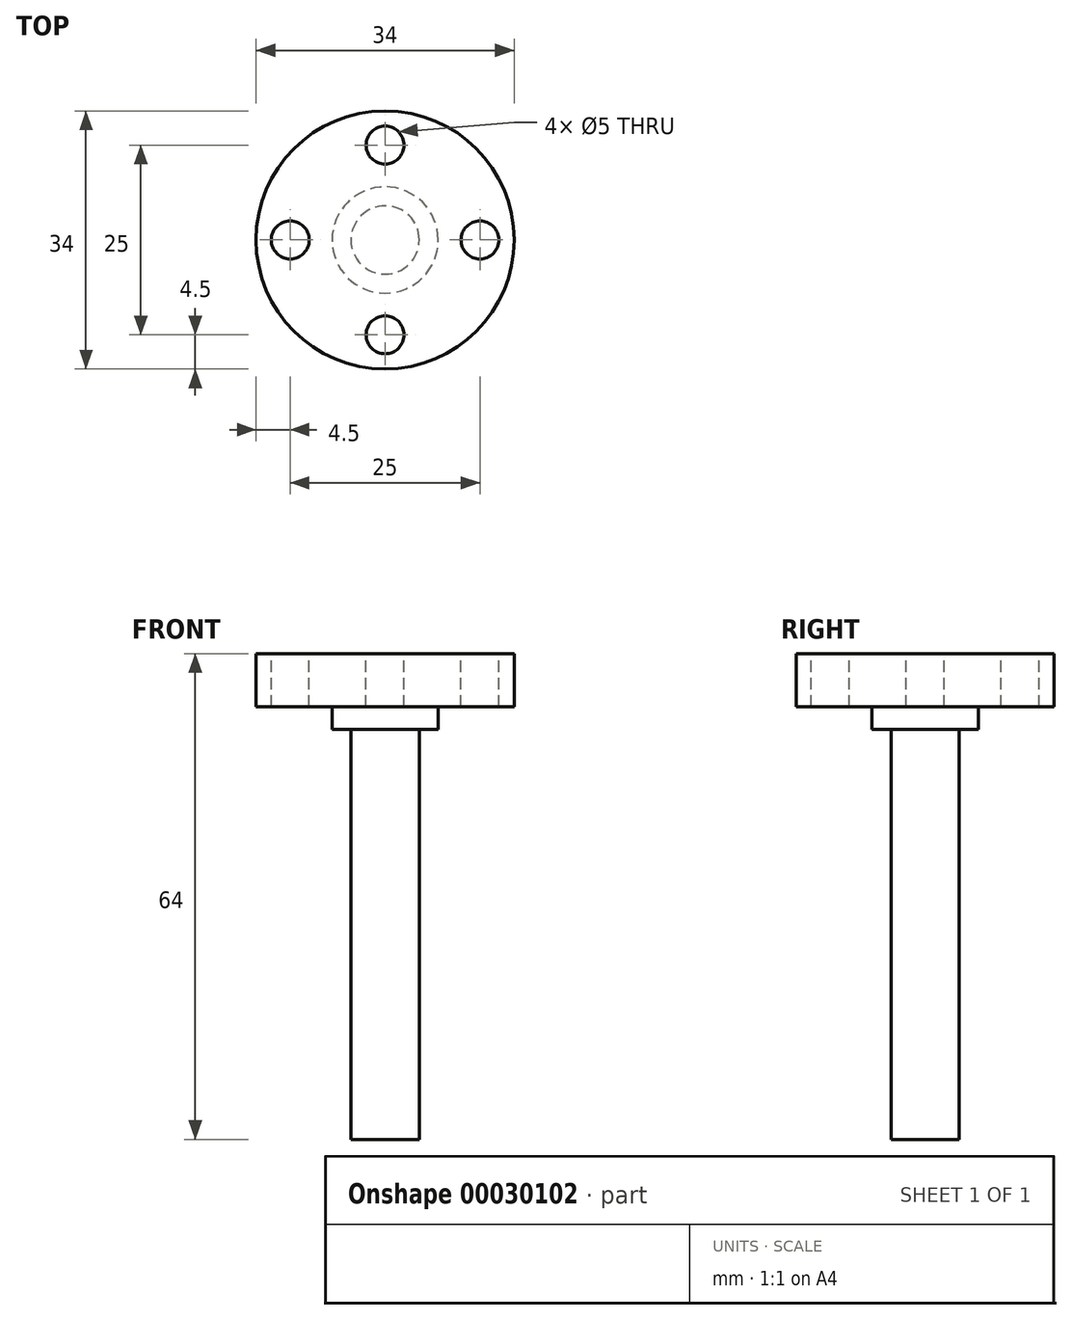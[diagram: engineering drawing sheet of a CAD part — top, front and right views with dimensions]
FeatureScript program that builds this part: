
annotation { "Feature Type Name" : "Feature", "Feature Type Description" : "" }
export const myFeature = defineFeature(function(context is Context, id is Id, definition is map)
    precondition{}
    {
        {
            var Q0;
            Q0=qCreatedBy(makeId("Right.planeOp"),FACE);
            var sketch = newSketch(context, id + "F0", { "sketchPlane" : qUnion([Q0])});
            skLineSegment(sketch, "E0", {"start": v(0, 0) * mm, "end": v(4.5, 0) * mm});
            skLineSegment(sketch, "E1", {"start": v(4.5, 0) * mm, "end": v(4.5, 54) * mm});
            skLineSegment(sketch, "E2", {"start": v(4.5, 54) * mm, "end": v(7, 54) * mm});
            skLineSegment(sketch, "E3", {"start": v(7, 54) * mm, "end": v(7, 57) * mm});
            skLineSegment(sketch, "E4", {"start": v(7, 57) * mm, "end": v(17, 57) * mm});
            skLineSegment(sketch, "E5", {"start": v(17, 57) * mm, "end": v(17, 64) * mm});
            skLineSegment(sketch, "E6", {"start": v(17, 64) * mm, "end": v(0, 64) * mm});
            skLineSegment(sketch, "E7", {"start": v(0, 64) * mm, "end": v(0, 0) * mm, "construction": true});
            skLineSegment(sketch, "E8", {"start": v(0, 64) * mm, "end": v(0, 0) * mm});
            skSolve(sketch);
        }
        {
            var Q0;
            Q0=makeQuery(id+"F0.imprint","IMPRINT",FACE,{"disambiguationData":[TD([[makeQuery(id+"F0.imprint","IMPRINT",EDGE,{"derivedFrom":sQuery(id+"F0.wireOp",EDGE,"E0")}),1.0]])]});
            var Q1;
            Q1=sQuery(id+"F0.wireOp",EDGE,"E8");
            revolve(context, id + "F1", {"entities" : qUnion([Q0]), "axis" : qUnion([Q1]), "revolveType" : RevolveType.FULL});
        }
        {
            var Q0;
            Q0=makeQuery(id+"F1.opRevolve","SWEPT_FACE",FACE,{"disambiguationData":[OSD([sQuery(id+"F0.wireOp",EDGE,"E6")])]});
            var sketch = newSketch(context, id + "F2", { "sketchPlane" : qUnion([Q0])});
            skCircle(sketch, "E9", {"center": v(0, 12.5) * mm, "radius": 2.25 * mm});
            skCircle(sketch, "E10", {"center": v(0, -12.5) * mm, "radius": 2.25 * mm});
            skCircle(sketch, "E11", {"center": v(12.5, 0) * mm, "radius": 2.25 * mm});
            skCircle(sketch, "E12", {"center": v(-12.5, 0) * mm, "radius": 2.25 * mm});
            skCircle(sketch, "E13", {"center": v(0, 0) * mm, "radius": 12.5 * mm, "construction": true});
            skSolve(sketch);
        }
        {
            var Q0;
            Q0=sQuery(id+"F2.wireOp",VERTEX,"E12.center");
            var Q1;
            Q1=sQuery(id+"F2.wireOp",VERTEX,"E10.center");
            var Q2;
            Q2=sQuery(id+"F2.wireOp",VERTEX,"E11.center");
            var Q3;
            Q3=sQuery(id+"F2.wireOp",VERTEX,"E9.center");
            var Q4;
            Q4=makeQuery(id+"F1.opRevolve","SWEPT_BODY",BODY,{"disambiguationData":[OSD([sQuery(id+"F0.wireOp",EDGE,"E0"),sQuery(id+"F0.wireOp",EDGE,"E1"),sQuery(id+"F0.wireOp",EDGE,"E2"),sQuery(id+"F0.wireOp",EDGE,"E3"),sQuery(id+"F0.wireOp",EDGE,"E4"),sQuery(id+"F0.wireOp",EDGE,"E5"),sQuery(id+"F0.wireOp",EDGE,"E6"),sQuery(id+"F0.wireOp",EDGE,"E8")])]});
            hole(context, id + "F3", {"style" : HoleStyle.SIMPLE, "holeDiameter" : 5 * mm, "endStyle" : HoleEndStyle.THROUGH, "locations" : qUnion([Q0, Q1, Q2, Q3]), "scope" : qUnion([Q4])});
        }
    });
